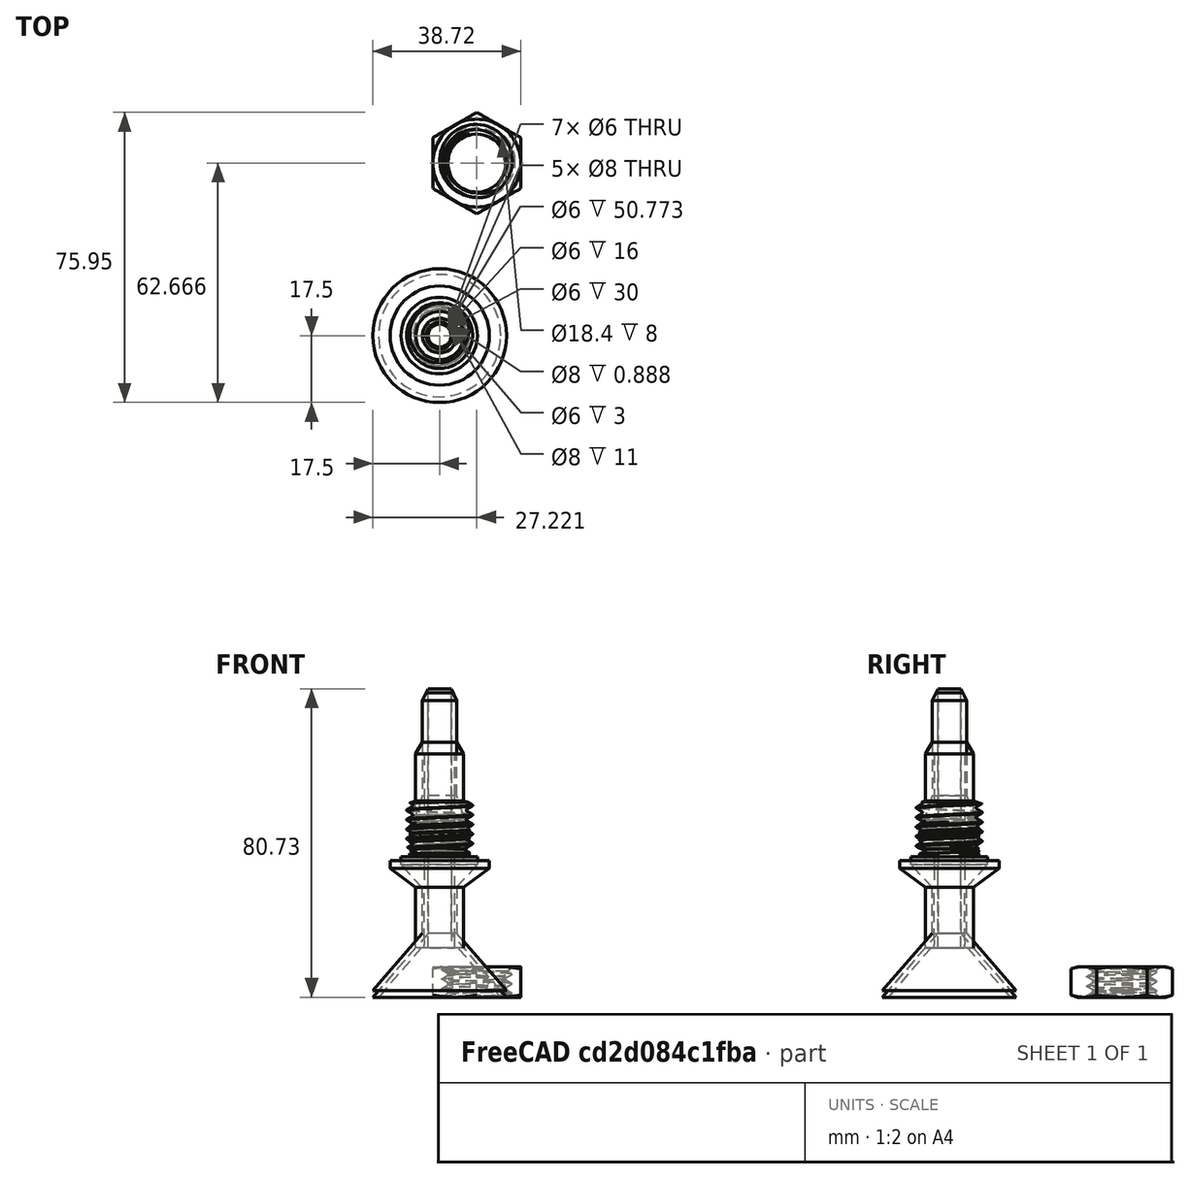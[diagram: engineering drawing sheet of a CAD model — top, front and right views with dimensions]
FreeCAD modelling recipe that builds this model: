
FCSTD DOCUMENT  (FreeCAD 0.18.4R)
Label: overflow-8.8_9.2
License: All rights reserved
LicenseURL: http://en.wikipedia.org/wiki/All_rights_reserved
objects: Part::Part2DObjectPython×19, Part::Extrusion×19, Part::MultiFuse×19, Part::Cut×18, Part::Feature×11, Part::FeaturePython×5, Part::Cone×3, App::DocumentObjectGroup×2
note: 94 computed .brp shape members not serialized (recipe doc carries the construction recipe); baked Part::Feature solids carry a one-line shape summary decoded from their .brp

FEATURE [Part::Feature] Cone  label="Cone006"
  Placement = pos=(-1.8e-15,0,10) rot=(0,0,1;0rad)
  shape: bbox 12.54 x 12.54 x 5 mm, 3 faces (baked)
FEATURE [Part::Feature] Extrusion005
  Placement = pos=(-1e-15,-3e-15,-24.4726) rot=(0,0,1;0rad)
  shape: bbox 6 x 6 x 97.89 mm, 3 faces (baked)
FEATURE [Part::Feature] Cone006  label="Cone008"
  Placement = pos=(-0.130628,0.000335684,-8) rot=(0,0,1;0rad)
  shape: bbox 20 x 20 x 5 mm, 3 faces (baked)
FEATURE [Part::Feature] Face
  shape: bbox 20 x 20 x 1e-05 mm, 1 faces, 0 solids (baked)
FEATURE [Part::Part2DObjectPython] Circle  # Draft 2D object (typed FeaturePython)
  FirstAngle = 0
  LastAngle = 0
  MakeFace = true
  Radius = 17.7
FEATURE [Part::Cut] Cut001  label="Screw"
FEATURE [Part::Feature] Cone005  label="Cone007"
  Placement = pos=(-0.163797,0.00042092,-7.5) rot=(0,0,1;0rad)
  shape: bbox 20 x 20 x 4.5 mm, 3 faces (baked)
FEATURE [Part::Extrusion] Extrusion009
  Base = -> Face
  Dir = (0,-1e-16,-1)
  DirMode = 0
  FaceMakerClass = Part::FaceMakerBullseye
  LengthFwd = 0
  LengthRev = 0
  Solid = true
  Symmetric = false
FEATURE [Part::Feature] Cone007  label="Cone009"
  Placement = pos=(-0.130628,0.000335684,-9) rot=(0,0,1;0rad)
  shape: bbox 20 x 20 x 6 mm, 3 faces (baked)
FEATURE [Part::Part2DObjectPython] Circle014  # Draft 2D object (typed FeaturePython)
  FirstAngle = 0
  LastAngle = 0
  MakeFace = true
  Placement = pos=(-24.5,-31.7831,-36) rot=(1,0,0;3.14159rad)
  Radius = 5.3
FEATURE [Part::Cut] Cut001004007  label="Nut-R=9,2"
  Placement = pos=(9.72081,45.166,-37.7308) rot=(0,0,1;0rad)
FEATURE [Part::Extrusion] Extrusion
  Base = -> Circle
  Dir = (0,0,-3)
  DirMode = 0
  FaceMakerClass = Part::FaceMakerBullseye
  LengthFwd = 0
  LengthRev = 0
  Solid = true
  Symmetric = false
FEATURE [Part::Part2DObjectPython] Circle001  # Draft 2D object (typed FeaturePython)
  FirstAngle = 0
  LastAngle = 0
  MakeFace = true
  Placement = pos=(0,-1e-15,-3) rot=(1,0,0;3.14159rad)
  Radius = 4.5
  Support = -> [Extrusion]
FEATURE [Part::Extrusion] Extrusion001
  Base = -> Circle001
  Dir = (0,0,-18)
  DirMode = 0
  FaceMakerClass = Part::FaceMakerBullseye
  LengthFwd = 0
  LengthRev = 0
  Solid = true
  Symmetric = false
FEATURE [Part::Part2DObjectPython] Circle003  # Draft 2D object (typed FeaturePython)
  FirstAngle = 0
  LastAngle = 0
  MakeFace = true
  Placement = pos=(0,0,10) rot=(0,0,1;0rad)
  Radius = 4.5
FEATURE [Part::Part2DObjectPython] Circle004  # Draft 2D object (typed FeaturePython)
  FirstAngle = 0
  LastAngle = 0
  MakeFace = true
  Placement = pos=(0,0,10) rot=(0,0,1;0rad)
  Radius = 3
  Support = -> [Circle003]
FEATURE [Part::Extrusion] Extrusion003
  Base = -> Circle004
  Dir = (0,0,30)
  DirMode = 0
  FaceMakerClass = Part::FaceMakerBullseye
  LengthFwd = 0
  LengthRev = 0
  Solid = true
  Symmetric = false
FEATURE [Part::Extrusion] Extrusion004
  Base = -> Circle003
  Dir = (0,0,30)
  DirMode = 0
  FaceMakerClass = Part::FaceMakerBullseye
  LengthFwd = 0
  LengthRev = 0
  Solid = true
  Symmetric = false
FEATURE [Part::MultiFuse] Fusion002
  Shapes = -> [Extrusion004,Cone]
FEATURE [Part::Part2DObjectPython] Circle007  # Draft 2D object (typed FeaturePython)
  FirstAngle = 0
  LastAngle = 0
  MakeFace = true
  Placement = pos=(-9e-16,-5.8e-15,40) rot=(0,0,1;0rad)
  Radius = 3
FEATURE [Part::Extrusion] Extrusion008
  Base = -> Circle007
  Dir = (0,0,-154.08)
  DirMode = 0
  FaceMakerClass = Part::FaceMakerBullseye
  LengthFwd = 0
  LengthRev = 0
  Solid = true
  Symmetric = false
FEATURE [Part::MultiFuse] Fusion009  label="ScrewBuiltIn"
  Placement = pos=(0,0,-1) rot=(0,0,1;0rad)
FEATURE [Part::Feature] Face001
  shape: bbox 26 x 26 x 1e-05 mm, 1 faces, 0 solids (baked)
FEATURE [Part::Part2DObjectPython] Rectangle  # Draft 2D object (typed FeaturePython)
  ChamferSize = 0
  Columns = 1
  FilletRadius = 0
  Height = 64.2364
  Length = 80.6682
  MakeFace = true
  Placement = pos=(-41.8567,-30.236,-1) rot=(0,0,1;0rad)
  Rows = 1
  Support = -> [Fusion009]
FEATURE [Part::MultiFuse] Fusion
  Shapes = -> [Extrusion001]
FEATURE [Part::MultiFuse] Fusion001
  Shapes = -> [Fusion,Extrusion]
FEATURE [Part::MultiFuse] Fusion003
  Shapes = -> [Fusion002,Fusion001]
FEATURE [Part::Cut] Cut002
  Base = -> Fusion003
  Tool = -> Extrusion005
FEATURE [Part::MultiFuse] Fusion004
  Shapes = -> [Cut002,Cut001]
FEATURE [Part::Part2DObjectPython] Circle002  # Draft 2D object (typed FeaturePython)
  FirstAngle = 0
  LastAngle = 0
  MakeFace = true
  Placement = pos=(1e-15,0,-21) rot=(1,0,0;3.14159rad)
  Radius = 3
  Support = -> [Fusion]
FEATURE [Part::Part2DObjectPython] Circle005  # Draft 2D object (typed FeaturePython)
  FirstAngle = 0
  LastAngle = 0
  MakeFace = true
  Placement = pos=(-0.130628,0.000335684,0) rot=(0,0,1;0rad)
  Radius = 25.0162
  Support = -> [Fusion004]
FEATURE [Part::Part2DObjectPython] Circle006  # Draft 2D object (typed FeaturePython)
  FirstAngle = 0
  LastAngle = 0
  MakeFace = true
  Placement = pos=(-0.130628,0.000335684,0) rot=(0,0,1;0rad)
  Radius = 10
  Support = -> [Fusion004]
FEATURE [Part::Extrusion] Extrusion006
  Base = -> Circle006
  Dir = (-4e-16,-1.5e-15,-14.2451)
  DirMode = 0
  FaceMakerClass = Part::FaceMakerBullseye
  LengthFwd = 0
  LengthRev = 0
  Solid = true
  Symmetric = false
FEATURE [Part::Extrusion] Extrusion007
  Base = -> Circle005
  Dir = (-4e-16,-1.5e-15,-14.2451)
  DirMode = 0
  FaceMakerClass = Part::FaceMakerBullseye
  LengthFwd = 0
  LengthRev = 0
  Solid = true
  Symmetric = false
FEATURE [Part::FeaturePython] Slice  # WARN: FeaturePython — macro-defined, semantics opaque (R4)
  Base = -> Fusion009
  Mode = 1
  Tolerance = 0
  Tools = -> [Rectangle]
FEATURE [Part::FeaturePython] Slice_child1  label="Slice.1"  # WARN: FeaturePython — macro-defined, semantics opaque (R4)
  Base = -> Slice
  FilterType = 1
  Invert = false
  OverrideMaxVal = 0
  Placement = pos=(0,0,-1) rot=(0,0,1;0rad)
  WindowFrom = 80
  WindowTo = 100
  items = 1
FEATURE [Part::FeaturePython] Slice_child0  label="Slice.0"  # WARN: FeaturePython — macro-defined, semantics opaque (R4)
  Base = -> Slice
  FilterType = 1
  Invert = false
  OverrideMaxVal = 0
  Placement = pos=(0,0,1) rot=(0,0,1;0rad)
  WindowFrom = 80
  WindowTo = 100
  items = 0
FEATURE [Part::Part2DObjectPython] Circle016  # Draft 2D object (typed FeaturePython)
  FirstAngle = 0
  LastAngle = 0
  MakeFace = true
  Placement = pos=(7e-15,0,-3) rot=(1,0,0;3.14159rad)
  Radius = 4
  Support = -> [Slice_child1]
FEATURE [Part::Extrusion] Extrusion014
  Base = -> Circle016
  Dir = (0,0,74)
  DirMode = 0
  FaceMakerClass = Part::FaceMakerBullseye
  LengthFwd = 0
  LengthRev = 0
  Solid = true
  Symmetric = false
FEATURE [Part::Cut] Cut003
  Base = -> Extrusion007
  Tool = -> Extrusion006
FEATURE [Part::Cut] Cut004
  Base = -> Fusion004
  Tool = -> Cut003
FEATURE [Part::MultiFuse] Fusion005
  Shapes = -> [Cut004,Cone005]
FEATURE [Part::Cut] Cut005
  Base = -> Fusion005
  Tool = -> Extrusion008
FEATURE [Part::Cut] Cut006
  Base = -> Cut005
  Tool = -> Extrusion009
FEATURE [Part::Part2DObjectPython] Circle009  # Draft 2D object (typed FeaturePython)
  FirstAngle = 0
  LastAngle = 0
  MakeFace = true
  Placement = pos=(-0.130628,0.000335684,-1) rot=(0,0,1;0rad)
  Radius = 7.79
  Support = -> [Cut006]
FEATURE [Part::Extrusion] Extrusion010
  Base = -> Circle009
  Dir = (0,0,1)
  DirMode = 0
  FaceMakerClass = Part::FaceMakerBullseye
  LengthFwd = 0
  LengthRev = 0
  Solid = true
  Symmetric = false
FEATURE [Part::MultiFuse] Fusion006
  Shapes = -> [Extrusion010,Cut006]
FEATURE [Part::Part2DObjectPython] Circle010  # Draft 2D object (typed FeaturePython)
  FirstAngle = 0
  LastAngle = 0
  MakeFace = true
  Placement = pos=(-9e-16,-5.8e-15,40) rot=(0,0,1;0rad)
  Radius = 3
  Support = -> [Fusion006]
FEATURE [Part::Extrusion] Extrusion011
  Base = -> Circle010
  Dir = (0,0,-177.512)
  DirMode = 0
  FaceMakerClass = Part::FaceMakerBullseye
  LengthFwd = 0
  LengthRev = 0
  Solid = true
  Symmetric = false
FEATURE [Part::MultiFuse] Fusion007
  Shapes = -> [Fusion006,Cone006]
FEATURE [Part::Cut] Cut007
  Base = -> Fusion007
  Tool = -> Extrusion011
FEATURE [Part::MultiFuse] Fusion008
  Shapes = -> [Cut007,Cone007]
FEATURE [Part::Part2DObjectPython] Circle012  # Draft 2D object (typed FeaturePython)
  FirstAngle = 0
  LastAngle = 0
  MakeFace = true
  Placement = pos=(-9e-16,-5.8e-15,40) rot=(0,0,1;0rad)
  Radius = 3
  Support = -> [Fusion008]
FEATURE [Part::Extrusion] Extrusion012
  Base = -> Circle012
  Dir = (0,0,-99.1538)
  DirMode = 0
  FaceMakerClass = Part::FaceMakerBullseye
  LengthFwd = 0
  LengthRev = 0
  Solid = true
  Symmetric = false
FEATURE [Part::Cut] Cut008
  Base = -> Fusion008
  Tool = -> Extrusion012
FEATURE [Part::Part2DObjectPython] Circle015  # Draft 2D object (typed FeaturePython)
  FirstAngle = 0
  LastAngle = 0
  MakeFace = true
  Placement = pos=(-9e-16,-5.8e-15,40) rot=(0,0,1;0rad)
  Radius = 6.27
  Support = -> [Cut008]
FEATURE [Part::Extrusion] Extrusion013
  Base = -> Circle015
  Dir = (0,0,-40)
  DirMode = 0
  FaceMakerClass = Part::FaceMakerBullseye
  LengthFwd = 0
  LengthRev = 0
  Placement = pos=(0,0,-2) rot=(0,0,1;0rad)
  Solid = true
  Symmetric = false
FEATURE [Part::Cut] Cut001004008
  Base = -> Extrusion013
  Placement = pos=(0,0,-2) rot=(0,0,1;0rad)
  Tool = -> Extrusion014
FEATURE [Part::Feature] Fusion010001  label="Fusion011"
  shape: bbox 12.54 x 12.54 x 20.77 mm, 4 faces (baked)
FEATURE [Part::Part2DObjectPython] Circle017  # Draft 2D object (typed FeaturePython)
  FirstAngle = 0
  LastAngle = 0
  MakeFace = true
  Placement = pos=(-7e-15,-1e-14,-24.7731) rot=(1,0,0;3.14159rad)
  Radius = 4
  Support = -> [Fusion010001]
FEATURE [Part::Extrusion] Extrusion019
  Base = -> Circle017
  Dir = (0,0,50.7731)
  DirMode = 0
  FaceMakerClass = Part::FaceMakerBullseye
  LengthFwd = 0
  LengthRev = 0
  Solid = true
  Symmetric = false
FEATURE [Part::Feature] Face004
  Placement = pos=(0,0,-2) rot=(0,0,1;0rad)
  shape: bbox 12.54 x 12.54 x 2e-07 mm, 1 faces, 0 solids (baked)
FEATURE [Part::Extrusion] Extrusion017
  Base = -> Face004
  Dir = (0,0,-10)
  DirMode = 0
  FaceMakerClass = Part::FaceMakerBullseye
  LengthFwd = 0
  LengthRev = 0
  Solid = true
  Symmetric = false
FEATURE [Part::Cut] Cut001004009
  Base = -> Cut001004008
  Tool = -> Extrusion017
FEATURE [Part::Cut] Cut001004011
  Placement = pos=(0,-1e-16,-1.73077) rot=(0,0,1;0rad)
  Tool = -> Extrusion019
FEATURE [Part::Extrusion] Extrusion015
  Dir = (0,0,-25)
  DirMode = 0
  FaceMakerClass = Part::FaceMakerBullseye
  LengthFwd = 0
  LengthRev = 0
  Solid = true
  Symmetric = false
FEATURE [Part::MultiFuse] Fusion010002
  Shapes = -> [Cut001004009,Fusion010001]
FEATURE [Part::Cone] Cone008  label="Cone010"
  Angle = 360
  AttacherType = Attacher::AttachEngine3D
  Height = 5
  Placement = pos=(0,0,-9) rot=(0,0,1;0rad)
  Radius1 = 6.27
  Radius2 = 13
FEATURE [Part::MultiFuse] Fusion010004
  Shapes = -> [Slice_child1,Cone008]
FEATURE [Part::Cut] Cut
  Placement = pos=(-74,42,-10.5) rot=(0,0,1;0rad)
FEATURE [Part::Cut] Cut001004012
  Base = -> Slice_child0
  Tool = -> Cut
FEATURE [Part::Cut] Cut001004013
  Placement = pos=(-74,-42,25) rot=(1,0,0;3.14159rad)
FEATURE [Part::Cut] Cut001004014
  Base = -> Cut001004012
  Tool = -> Cut001004013
FEATURE [Part::Cone] Cone001
  Angle = 360
  AttacherType = Attacher::AttachEngine3D
  Height = 3
  Placement = pos=(0,-7.1e-15,26) rot=(0,0,1;0rad)
  Radius1 = 6.27
  Radius2 = 4.5
FEATURE [Part::MultiFuse] Fusion010005
  Shapes = -> [Fusion010002,Cone001]
FEATURE [Part::Cone] Cone009  label="Cone011"
  Angle = 360
  AttacherType = Attacher::AttachEngine3D
  Height = 3
  Placement = pos=(0,0,40) rot=(0,0,1;0rad)
  Radius1 = 4.5
  Radius2 = 3
FEATURE [Part::MultiFuse] Fusion010006
  Shapes = -> [Extrusion015,Cone009]
FEATURE [Part::MultiFuse] Fusion010007
  Shapes = -> [Fusion010006,Fusion010005]
FEATURE [Part::MultiFuse] Fusion010008
  Shapes = -> [Fusion010007,Cut001004011]
FEATURE [Part::Part2DObjectPython] Circle018  # Draft 2D object (typed FeaturePython)
  FirstAngle = 0
  LastAngle = 0
  MakeFace = true
  Placement = pos=(1e-15,0,43) rot=(0,0,1;0rad)
  Radius = 3
  Support = -> [Fusion010008]
FEATURE [Part::Extrusion] Extrusion020
  Base = -> Circle018
  Dir = (0,0,-111)
  DirMode = 0
  FaceMakerClass = Part::FaceMakerBullseye
  LengthFwd = 0
  LengthRev = 0
  Solid = true
  Symmetric = false
FEATURE [Part::MultiFuse] Fusion010009
  Shapes = -> [Fusion010004,Fusion010008]
FEATURE [Part::Cut] Cut001004015
  Base = -> Fusion010009
  Tool = -> Extrusion020
FEATURE [Part::Part2DObjectPython] Circle019  # Draft 2D object (typed FeaturePython)
  FirstAngle = 0
  LastAngle = 0
  MakeFace = true
  Placement = pos=(-2.1e-14,-1e-15,-24.7731) rot=(1,0,0;3.14159rad)
  Radius = 4
  Support = -> [Cut001004015]
FEATURE [Part::Extrusion] Extrusion021
  Base = -> Circle019
  Dir = (0,0,50.7731)
  DirMode = 0
  FaceMakerClass = Part::FaceMakerBullseye
  LengthFwd = 0
  LengthRev = 0
  Solid = true
  Symmetric = false
FEATURE [Part::Cut] Cut001004016
  Base = -> Cut001004015
  Tool = -> Extrusion021
FEATURE [Part::Feature] Cut001004016001  label="Cut001004017"
  shape: bbox 35 x 35 x 80.73 mm, 15 faces (baked)
FEATURE [Part::MultiFuse] Fusion010010
  Shapes = -> [Cut001004016001,Cut001004014]
FEATURE [App::DocumentObjectGroup] GrExplode_Slice  label="Exploded Slice"
  Group = -> [Cut001004016,Fusion010010]
FEATURE [Part::Part2DObjectPython] Rectangle001  # Draft 2D object (typed FeaturePython)
  ChamferSize = 0
  Columns = 1
  FilletRadius = 0
  Height = 66
  Length = 62
  MakeFace = true
  Placement = pos=(-28,-33,42) rot=(0,0,1;0rad)
  Rows = 1
  Support = -> [Fusion010010]
FEATURE [Part::FeaturePython] Slice001  # WARN: FeaturePython — macro-defined, semantics opaque (R4)
  Base = -> Fusion010010
  Mode = 1
  Tolerance = 0
  Tools = -> [Rectangle001]
FEATURE [Part::FeaturePython] Slice001_child0  label="Slice001.0"  # WARN: FeaturePython — macro-defined, semantics opaque (R4)
  Base = -> Slice001
  FilterType = 1
  Invert = false
  OverrideMaxVal = 0
  WindowFrom = 80
  WindowTo = 100
  items = 0
FEATURE [Part::Feature] Face005
  shape: bbox 8 x 8 x 2e-07 mm, 1 faces, 0 solids (baked)
FEATURE [Part::Extrusion] Extrusion022
  Base = -> Face005
  Dir = (0,0,-50.7731)
  DirMode = 0
  FaceMakerClass = Part::FaceMakerBullseye
  LengthFwd = 0
  LengthRev = 0
  Solid = true
  Symmetric = false
FEATURE [Part::MultiFuse] Fusion010011
  Shapes = -> [Slice001_child0,Extrusion022]
FEATURE [App::DocumentObjectGroup] GrExplode_Slice001  label="Tube-8,8"
  Group = -> [Fusion010011]
